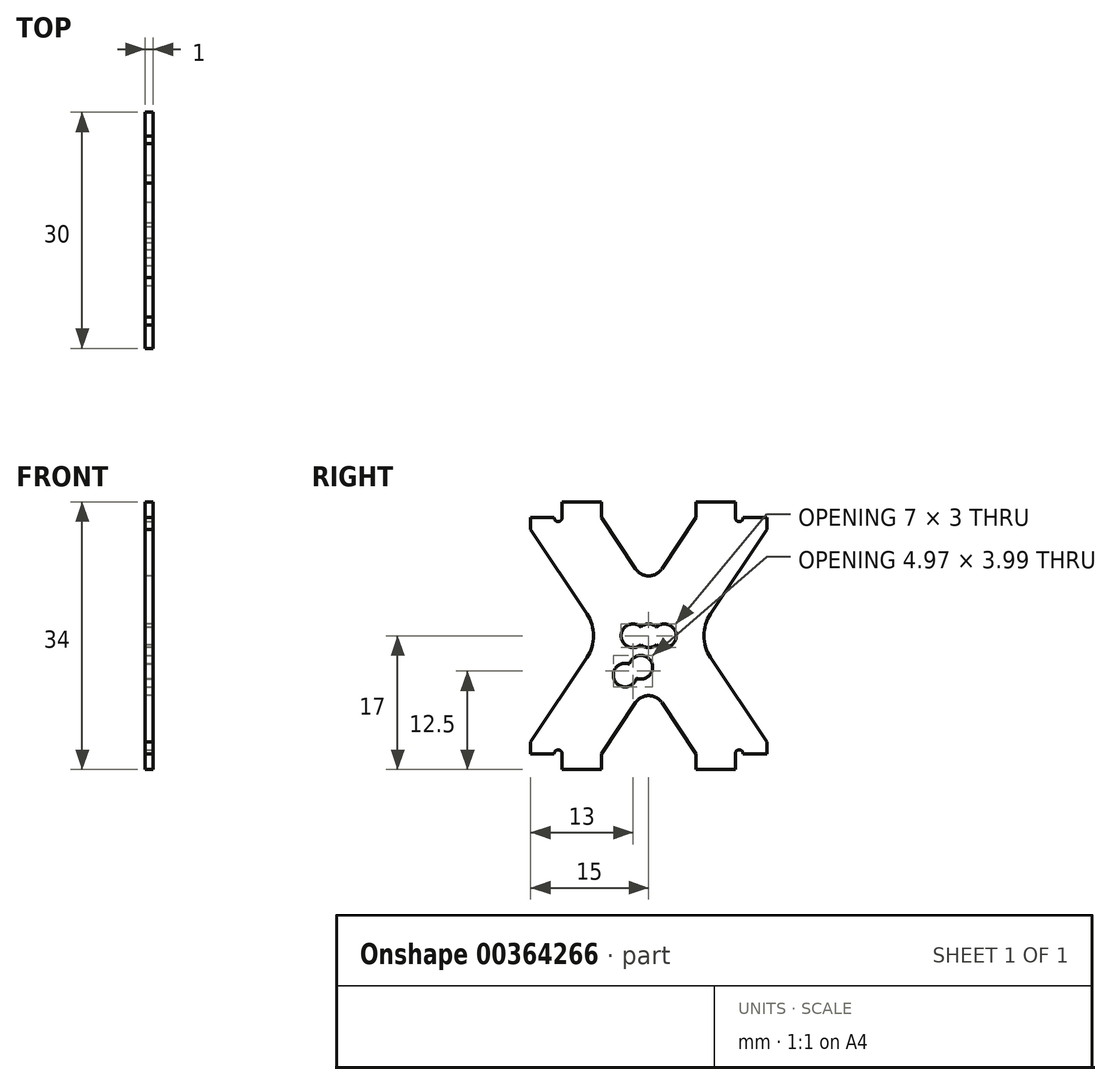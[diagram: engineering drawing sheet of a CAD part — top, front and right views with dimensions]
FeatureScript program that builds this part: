
annotation { "Feature Type Name" : "Feature", "Feature Type Description" : "" }
export const myFeature = defineFeature(function(context is Context, id is Id, definition is map)
    precondition{}
    {
        {
            var Q0;
            Q0=qCreatedBy(makeId("Right.planeOp"),FACE);
            var sketch = newSketch(context, id + "F0", { "sketchPlane" : qUnion([Q0])});
            skLineSegment(sketch, "E0.bottom", {"start": v(-11, 17) * mm, "end": v(-6, 17) * mm});
            skLineSegment(sketch, "E0.left", {"start": v(-11, 17) * mm, "end": v(-11, 0) * mm});
            skLineSegment(sketch, "E0.right", {"start": v(11, 17) * mm, "end": v(11, 0) * mm});
            skLineSegment(sketch, "E1.left", {"start": v(-6, 17) * mm, "end": v(-6, 15) * mm});
            skLineSegment(sketch, "E1.right", {"start": v(6, 17) * mm, "end": v(6, 15) * mm});
            skLineSegment(sketch, "E2.trimOffspring", {"start": v(6, 17) * mm, "end": v(11, 17) * mm});
            skLineSegment(sketch, "E3", {"start": v(-11, 0) * mm, "end": v(11, 0) * mm, "construction": true});
            skCircle(sketch, "E4", {"center": v(-2, 0) * mm, "radius": 1.5 * mm});
            skCircle(sketch, "E5", {"center": v(2, 0) * mm, "radius": 1.5 * mm});
            skLineSegment(sketch, "E6.MirrorCS", {"start": v(6, -17) * mm, "end": v(6, -15) * mm});
            skLineSegment(sketch, "E7.MirrorCS", {"start": v(-6, -17) * mm, "end": v(-6, -15) * mm});
            skLineSegment(sketch, "E8.MirrorCS", {"start": v(6, -17) * mm, "end": v(11, -17) * mm});
            skLineSegment(sketch, "E9.MirrorCS", {"start": v(-11, -17) * mm, "end": v(-6, -17) * mm});
            skLineSegment(sketch, "E10.MirrorCS", {"start": v(11, -17) * mm, "end": v(11, 0) * mm});
            skLineSegment(sketch, "E11.MirrorCS", {"start": v(-11, -17) * mm, "end": v(-11, 0) * mm});
            skLineSegment(sketch, "E12", {"start": v(-6, 15) * mm, "end": v(-1.66, 8.5) * mm});
            skPoint(sketch, "E13.trimOffspring.end.orphan", {"position": v(6, 15) * mm});
            skLineSegment(sketch, "E14.MirrorCS", {"start": v(6, 15) * mm, "end": v(1.66, 8.5) * mm});
            skLineSegment(sketch, "E15.MirrorCS", {"start": v(-6, -15) * mm, "end": v(-1.66, -8.5) * mm});
            skLineSegment(sketch, "E16.MirrorCS", {"start": v(6, -15) * mm, "end": v(1.66, -8.5) * mm});
            skPoint(sketch, "E17.MirrorCS.end.orphan", {"position": v(6, -15) * mm});
            skPoint(sketch, "E17.MirrorCS.start.orphan", {"position": v(-6, -15) * mm});
            skPoint(sketch, "E18.visualSharp", {"position": v(0, -6) * mm});
            skArc(sketch, "E18.filletArc", {"start": v(1.66, -8.5) * mm, "mid": v(0, -7.6) * mm, "end": v(-1.66, -8.5) * mm});
            skPoint(sketch, "E19.visualSharp", {"position": v(0, 6) * mm});
            skArc(sketch, "E19.filletArc", {"start": v(-1.66, 8.5) * mm, "mid": v(0, 7.6) * mm, "end": v(1.66, 8.5) * mm});
            skSolve(sketch);
        }
        {
            var Q0;
            Q0=makeQuery(id+"F0.imprint","IMPRINT",FACE,{"disambiguationData":[TD([[makeQuery(id+"F0.imprint","IMPRINT",EDGE,{"derivedFrom":sQuery(id+"F0.wireOp",EDGE,"E0.bottom")}),-1.0]])]});
            extrude(context, id + "F1", {"entities" : qUnion([Q0]), "depth" : 1 * mm});
        }
        {
            var Q0;
            Q0=makeQuery(id+"F1.opExtrude","SWEPT_FACE",FACE,{"disambiguationData":[OSD([sQuery(id+"F0.wireOp",EDGE,"E0.left"),sQuery(id+"F0.wireOp",EDGE,"E11.MirrorCS")])]});
            var sketch = newSketch(context, id + "F2", { "sketchPlane" : qUnion([Q0])});
            skLineSegment(sketch, "E20.bottom", {"start": v(0, 15) * mm, "end": v(1, 15) * mm});
            skLineSegment(sketch, "E20.top", {"start": v(0, -15) * mm, "end": v(1, -15) * mm});
            skLineSegment(sketch, "E20.left", {"start": v(0, 15) * mm, "end": v(0, -15) * mm});
            skLineSegment(sketch, "E20.right", {"start": v(1, 15) * mm, "end": v(1, -15) * mm});
            skSolve(sketch);
        }
        {
            var Q0;
            Q0 = qSketchRegion(id + "F2", true);
            extrude(context, id + "F3", {"entities" : qUnion([Q0]), "operationType" : NewBodyOperationType.ADD, "depth" : 5 * mm});
        }
        {
            var Q0;
            Q0=makeQuery(id+"F1.opExtrude","SWEPT_FACE",FACE,{"disambiguationData":[OSD([sQuery(id+"F0.wireOp",EDGE,"E0.right"),sQuery(id+"F0.wireOp",EDGE,"E10.MirrorCS")])]});
            var sketch = newSketch(context, id + "F4", { "sketchPlane" : qUnion([Q0])});
            skLineSegment(sketch, "E21.bottom", {"start": v(-1, 15) * mm, "end": v(0, 15) * mm});
            skLineSegment(sketch, "E21.top", {"start": v(-1, -15) * mm, "end": v(0, -15) * mm});
            skLineSegment(sketch, "E21.left", {"start": v(-1, 15) * mm, "end": v(-1, -15) * mm});
            skLineSegment(sketch, "E21.right", {"start": v(0, 15) * mm, "end": v(0, -15) * mm});
            skSolve(sketch);
        }
        {
            var Q0;
            Q0 = qSketchRegion(id + "F4", true);
            extrude(context, id + "F5", {"entities" : qUnion([Q0]), "operationType" : NewBodyOperationType.ADD, "depth" : 5 * mm});
        }
        {
            var Q0;
            Q0=makeQuery(id+"F5.boolean.opBoolean","MERGE",FACE,{"derivedFrom":[makeQuery(id+"F3.boolean.opBoolean","MERGE",FACE,{"derivedFrom":[makeQuery(id+"F1.opExtrude","CAP_FACE",FACE,{"disambiguationData":[OSD([sQuery(id+"F0.wireOp",EDGE,"E0.bottom"),sQuery(id+"F0.wireOp",EDGE,"E0.left"),sQuery(id+"F0.wireOp",EDGE,"E0.right"),sQuery(id+"F0.wireOp",EDGE,"E1.left"),sQuery(id+"F0.wireOp",EDGE,"E1.right"),sQuery(id+"F0.wireOp",EDGE,"E2.trimOffspring"),sQuery(id+"F0.wireOp",EDGE,"6mr2IOkQ-MI1l-MyX0-CG9S-OfoUgUFhcACP"),sQuery(id+"F0.wireOp",EDGE,"E4"),sQuery(id+"F0.wireOp",EDGE,"E5"),sQuery(id+"F0.wireOp",EDGE,"4yzbbwpy-ojnn-uAqB-lGtc-izO3n3sG2pIL"),sQuery(id+"F0.wireOp",EDGE,"hm3e2eem-uvXd-jqkw-lENi-lVE8c0etyPoi"),sQuery(id+"F0.wireOp",EDGE,"E13.trimOffspring"),sQuery(id+"F0.wireOp",EDGE,"afe5def2-a660-461b-9af6-917fafb5b7120.MirrorCS"),sQuery(id+"F0.wireOp",EDGE,"dee7cb01-9c4b-4eca-b62a-32f93c3b95220.MirrorCS"),sQuery(id+"F0.wireOp",EDGE,"dee7cb01-9c4b-4eca-b62a-32f93c3b95221.MirrorCS"),sQuery(id+"F0.wireOp",EDGE,"E6.MirrorCS"),sQuery(id+"F0.wireOp",EDGE,"E7.MirrorCS"),sQuery(id+"F0.wireOp",EDGE,"E8.MirrorCS"),sQuery(id+"F0.wireOp",EDGE,"E17.MirrorCS"),sQuery(id+"F0.wireOp",EDGE,"E9.MirrorCS"),sQuery(id+"F0.wireOp",EDGE,"E10.MirrorCS"),sQuery(id+"F0.wireOp",EDGE,"E11.MirrorCS")])],"isStart":false}),makeQuery(id+"F3.opExtrude","SWEPT_FACE",FACE,{"disambiguationData":[OSD([sQuery(id+"F2.wireOp",EDGE,"E20.right")])]})]}),makeQuery(id+"F5.opExtrude","SWEPT_FACE",FACE,{"disambiguationData":[OSD([sQuery(id+"F4.wireOp",EDGE,"E21.left")])]})]});
            var sketch = newSketch(context, id + "F6", { "sketchPlane" : qUnion([Q0])});
            skCircle(sketch, "E22", {"center": v(-11.5, 15) * mm, "radius": 0.5 * mm});
            skCircle(sketch, "E23.MirrorC", {"center": v(11.5, 15) * mm, "radius": 0.5 * mm});
            skCircle(sketch, "E24.MirrorC", {"center": v(-11.5, -15) * mm, "radius": 0.5 * mm});
            skCircle(sketch, "E25.MirrorC", {"center": v(11.5, -15) * mm, "radius": 0.5 * mm});
            skSolve(sketch);
        }
        {
            var Q0;
            Q0 = qSketchRegion(id + "F6", true);
            extrude(context, id + "F7", {"entities" : qUnion([Q0]), "operationType" : NewBodyOperationType.REMOVE, "oppositeDirection" : true, "depth" : 25 * mm});
        }
        {
            var Q0;
            Q0=makeQuery(id+"F5.boolean.opBoolean","MERGE",FACE,{"derivedFrom":[makeQuery(id+"F3.boolean.opBoolean","MERGE",FACE,{"derivedFrom":[makeQuery(id+"F1.opExtrude","CAP_FACE",FACE,{"disambiguationData":[OSD([sQuery(id+"F0.wireOp",EDGE,"E0.bottom"),sQuery(id+"F0.wireOp",EDGE,"E0.left"),sQuery(id+"F0.wireOp",EDGE,"E0.right"),sQuery(id+"F0.wireOp",EDGE,"E1.left"),sQuery(id+"F0.wireOp",EDGE,"E1.right"),sQuery(id+"F0.wireOp",EDGE,"E2.trimOffspring"),sQuery(id+"F0.wireOp",EDGE,"E4"),sQuery(id+"F0.wireOp",EDGE,"E5"),sQuery(id+"F0.wireOp",EDGE,"E6.MirrorCS"),sQuery(id+"F0.wireOp",EDGE,"E7.MirrorCS"),sQuery(id+"F0.wireOp",EDGE,"E8.MirrorCS"),sQuery(id+"F0.wireOp",EDGE,"E9.MirrorCS"),sQuery(id+"F0.wireOp",EDGE,"E10.MirrorCS"),sQuery(id+"F0.wireOp",EDGE,"E11.MirrorCS"),sQuery(id+"F0.wireOp",EDGE,"E12"),sQuery(id+"F0.wireOp",EDGE,"E14.MirrorCS"),sQuery(id+"F0.wireOp",EDGE,"E15.MirrorCS"),sQuery(id+"F0.wireOp",EDGE,"E16.MirrorCS"),sQuery(id+"F0.wireOp",EDGE,"E18.filletArc"),sQuery(id+"F0.wireOp",EDGE,"E19.filletArc")])],"isStart":false}),makeQuery(id+"F3.opExtrude","SWEPT_FACE",FACE,{"disambiguationData":[OSD([sQuery(id+"F2.wireOp",EDGE,"E20.right")])]})]}),makeQuery(id+"F5.opExtrude","SWEPT_FACE",FACE,{"disambiguationData":[OSD([sQuery(id+"F4.wireOp",EDGE,"E21.left")])]})]});
            var sketch = newSketch(context, id + "F8", { "sketchPlane" : qUnion([Q0])});
            skLineSegment(sketch, "E26", {"start": v(-16, 15) * mm, "end": v(-7.85, 2.77) * mm});
            skLineSegment(sketch, "E27", {"start": v(-7.85, -2.77) * mm, "end": v(-16, -15) * mm});
            skPoint(sketch, "E28.visualSharp", {"position": v(-6, 0) * mm});
            skArc(sketch, "E28.filletArc", {"start": v(-7.85, -2.77) * mm, "mid": v(-7, 0) * mm, "end": v(-7.85, 2.77) * mm});
            skLineSegment(sketch, "E29", {"start": v(-16, 15) * mm, "end": v(-16, -15) * mm});
            skLineSegment(sketch, "E30", {"start": v(16, 15) * mm, "end": v(7.85, 2.77) * mm});
            skLineSegment(sketch, "E31", {"start": v(7.85, -2.77) * mm, "end": v(16, -15) * mm});
            skLineSegment(sketch, "E32", {"start": v(16, 15) * mm, "end": v(16, -15) * mm});
            skPoint(sketch, "E33.visualSharp", {"position": v(6, 0) * mm});
            skArc(sketch, "E33.filletArc", {"start": v(7.85, 2.77) * mm, "mid": v(7, 0) * mm, "end": v(7.85, -2.77) * mm});
            skSolve(sketch);
        }
        {
            var Q0;
            Q0 = qSketchRegion(id + "F8", true);
            extrude(context, id + "F9", {"entities" : qUnion([Q0]), "operationType" : NewBodyOperationType.REMOVE, "oppositeDirection" : true, "depth" : 25 * mm});
        }
        {
            var Q0;
            Q0=makeQuery(id+"F5.boolean.opBoolean","MERGE",FACE,{"derivedFrom":[makeQuery(id+"F3.boolean.opBoolean","MERGE",FACE,{"derivedFrom":[makeQuery(id+"F1.opExtrude","CAP_FACE",FACE,{"disambiguationData":[OSD([sQuery(id+"F0.wireOp",EDGE,"E0.bottom"),sQuery(id+"F0.wireOp",EDGE,"E0.left"),sQuery(id+"F0.wireOp",EDGE,"E0.right"),sQuery(id+"F0.wireOp",EDGE,"E1.left"),sQuery(id+"F0.wireOp",EDGE,"E1.right"),sQuery(id+"F0.wireOp",EDGE,"E2.trimOffspring"),sQuery(id+"F0.wireOp",EDGE,"E4"),sQuery(id+"F0.wireOp",EDGE,"E5"),sQuery(id+"F0.wireOp",EDGE,"E6.MirrorCS"),sQuery(id+"F0.wireOp",EDGE,"E7.MirrorCS"),sQuery(id+"F0.wireOp",EDGE,"E8.MirrorCS"),sQuery(id+"F0.wireOp",EDGE,"E9.MirrorCS"),sQuery(id+"F0.wireOp",EDGE,"E10.MirrorCS"),sQuery(id+"F0.wireOp",EDGE,"E11.MirrorCS"),sQuery(id+"F0.wireOp",EDGE,"E12"),sQuery(id+"F0.wireOp",EDGE,"E14.MirrorCS"),sQuery(id+"F0.wireOp",EDGE,"E15.MirrorCS"),sQuery(id+"F0.wireOp",EDGE,"E16.MirrorCS"),sQuery(id+"F0.wireOp",EDGE,"E18.filletArc"),sQuery(id+"F0.wireOp",EDGE,"E19.filletArc")])],"isStart":false}),makeQuery(id+"F3.opExtrude","SWEPT_FACE",FACE,{"disambiguationData":[OSD([sQuery(id+"F2.wireOp",EDGE,"E20.right")])]})]}),makeQuery(id+"F5.opExtrude","SWEPT_FACE",FACE,{"disambiguationData":[OSD([sQuery(id+"F4.wireOp",EDGE,"E21.left")])]})]});
            var sketch = newSketch(context, id + "F10", { "sketchPlane" : qUnion([Q0])});
            skLineSegment(sketch, "E34", {"start": v(-15, 17.5) * mm, "end": v(-15, -17.5) * mm});
            skLineSegment(sketch, "E35", {"start": v(-15, -17.5) * mm, "end": v(-20, -17.5) * mm});
            skLineSegment(sketch, "E36", {"start": v(-20, -17.5) * mm, "end": v(-20, 17.5) * mm});
            skLineSegment(sketch, "E37", {"start": v(-20, 17.5) * mm, "end": v(-15, 17.5) * mm});
            skLineSegment(sketch, "E38.MirrorCS", {"start": v(20, 17.5) * mm, "end": v(15, 17.5) * mm});
            skLineSegment(sketch, "E39.MirrorCS", {"start": v(20, -17.5) * mm, "end": v(20, 17.5) * mm});
            skLineSegment(sketch, "E40.MirrorCS", {"start": v(15, 17.5) * mm, "end": v(15, -17.5) * mm});
            skLineSegment(sketch, "E41.MirrorCS", {"start": v(15, -17.5) * mm, "end": v(20, -17.5) * mm});
            skSolve(sketch);
        }
        {
            var Q0;
            Q0 = qSketchRegion(id + "F10", true);
            extrude(context, id + "F11", {"entities" : qUnion([Q0]), "operationType" : NewBodyOperationType.REMOVE, "oppositeDirection" : true, "depth" : 25 * mm});
        }
        {
            var Q0;
            Q0=makeQuery(id+"F5.boolean.opBoolean","MERGE",FACE,{"derivedFrom":[makeQuery(id+"F3.boolean.opBoolean","MERGE",FACE,{"derivedFrom":[makeQuery(id+"F1.opExtrude","CAP_FACE",FACE,{"disambiguationData":[OSD([sQuery(id+"F0.wireOp",EDGE,"E0.bottom"),sQuery(id+"F0.wireOp",EDGE,"E0.left"),sQuery(id+"F0.wireOp",EDGE,"E0.right"),sQuery(id+"F0.wireOp",EDGE,"E1.left"),sQuery(id+"F0.wireOp",EDGE,"E1.right"),sQuery(id+"F0.wireOp",EDGE,"E2.trimOffspring"),sQuery(id+"F0.wireOp",EDGE,"E4"),sQuery(id+"F0.wireOp",EDGE,"E5"),sQuery(id+"F0.wireOp",EDGE,"E6.MirrorCS"),sQuery(id+"F0.wireOp",EDGE,"E7.MirrorCS"),sQuery(id+"F0.wireOp",EDGE,"E8.MirrorCS"),sQuery(id+"F0.wireOp",EDGE,"E9.MirrorCS"),sQuery(id+"F0.wireOp",EDGE,"E10.MirrorCS"),sQuery(id+"F0.wireOp",EDGE,"E11.MirrorCS"),sQuery(id+"F0.wireOp",EDGE,"E12"),sQuery(id+"F0.wireOp",EDGE,"E14.MirrorCS"),sQuery(id+"F0.wireOp",EDGE,"E15.MirrorCS"),sQuery(id+"F0.wireOp",EDGE,"E16.MirrorCS"),sQuery(id+"F0.wireOp",EDGE,"E18.filletArc"),sQuery(id+"F0.wireOp",EDGE,"E19.filletArc")])],"isStart":false}),makeQuery(id+"F3.opExtrude","SWEPT_FACE",FACE,{"disambiguationData":[OSD([sQuery(id+"F2.wireOp",EDGE,"E20.right")])]})]}),makeQuery(id+"F5.opExtrude","SWEPT_FACE",FACE,{"disambiguationData":[OSD([sQuery(id+"F4.wireOp",EDGE,"E21.left")])]})]});
            var sketch = newSketch(context, id + "F12", { "sketchPlane" : qUnion([Q0])});
            skCircle(sketch, "E42", {"center": v(0, 0) * mm, "radius": 1.5 * mm});
            skArc(sketch, "E43", {"start": v(-1.55, -5.4) * mm, "mid": v(0.34, -3.33) * mm, "end": v(-2.45, -3.6) * mm});
            skArc(sketch, "E44", {"start": v(-2.45, -3.6) * mm, "mid": v(-4.34, -5.67) * mm, "end": v(-1.55, -5.4) * mm});
            skSolve(sketch);
        }
        {
            var Q0;
            Q0 = qSketchRegion(id + "F12", true);
            extrude(context, id + "F13", {"entities" : qUnion([Q0]), "operationType" : NewBodyOperationType.REMOVE, "oppositeDirection" : true, "depth" : 25 * mm});
        }
    });
